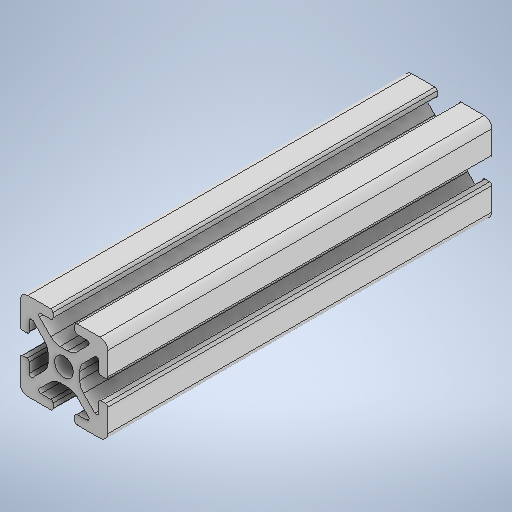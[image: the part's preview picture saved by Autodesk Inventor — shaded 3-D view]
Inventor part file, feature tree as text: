
AUTODESK INVENTOR PART (.ipt)
format: ipt  version: 2025.1 (Build 291241000, 241)  size: 425,472 bytes
history: native  units: in
note: dims shown in document units (in); Inventor stores cm internally (conversion verified against a paired STEP export)
features: mirror x1, direct_edit x1, extrude x1, sketch x1, projected_geometry x1, move_body x1
ambient origin geometry x8: Origin, YZ Plane, XZ Plane, XY Plane, X Axis, Y Axis, Z Axis, Center Point
bodies: Solid1 (feature_tree)
feature tree (6):
  mirror  "Mirror2"
  direct_edit  "Direct Edit2"
  extrude  "Extrusion1"  Depth=0.125in TaperAngle=0.0deg
  sketch  "Sketch1"  dims[d3=0.0in d4=0.0in d5=3.33in d6=0.125in d7=0.0in]
  projected_geometry  "Projected Loop1"
  move_body  "Move2"
